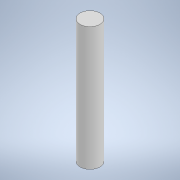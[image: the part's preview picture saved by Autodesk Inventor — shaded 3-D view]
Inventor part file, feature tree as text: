
AUTODESK INVENTOR PART (.ipt)
format: ipt  version: 2021 (Build 250183000, 183)  size: 89,600 bytes
history: native  units: mm
features: extrude x1, sketch x1
ambient origin geometry x8: Origin, YZ Plane, XZ Plane, XY Plane, X Axis, Y Axis, Z Axis, Center Point
bodies: Solid1 (feature_tree)
feature tree (2):
  extrude  "Extrusion1"  Depth=50.0mm TaperAngle=0.0deg
  sketch  "Sketch1"  dims[d0=8.0mm d1=50.0mm d2=0.0mm]
